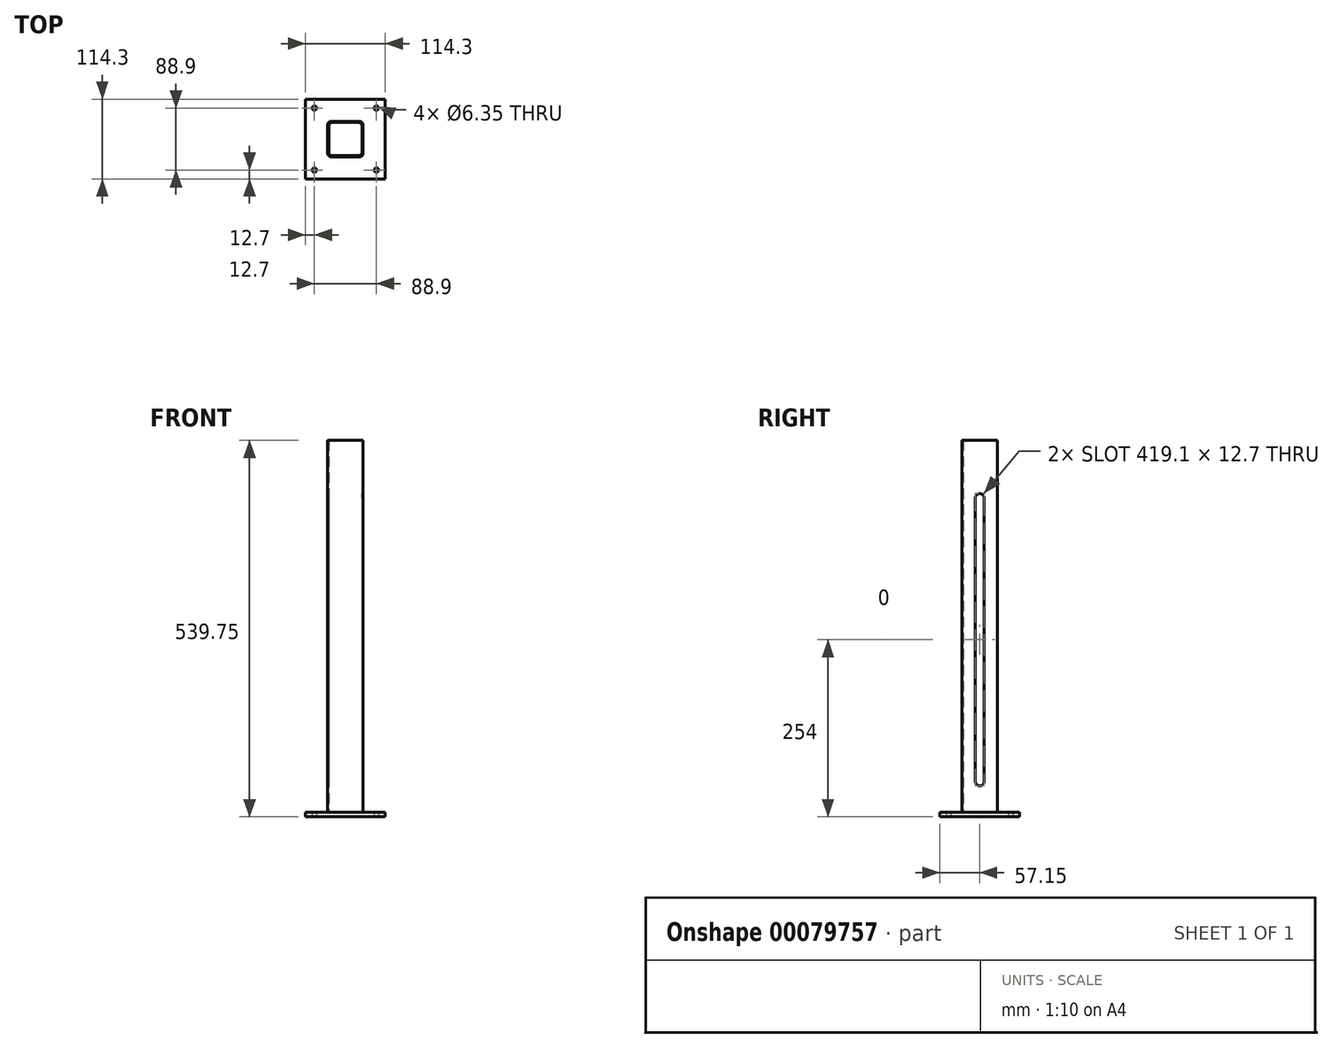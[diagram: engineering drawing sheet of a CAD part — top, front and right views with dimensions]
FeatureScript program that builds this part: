
annotation { "Feature Type Name" : "Feature", "Feature Type Description" : "" }
export const myFeature = defineFeature(function(context is Context, id is Id, definition is map)
    precondition{}
    {
        {
            var Q0;
            Q0=qCreatedBy(makeId("Top.planeOp"),FACE);
            var sketch = newSketch(context, id + "F0", { "sketchPlane" : qUnion([Q0])});
            skPoint(sketch, "E0.middle", {"position": v(0, 0) * mm});
            skCircle(sketch, "E1", {"center": v(-44.45, 44.45) * mm, "radius": 3.18 * mm});
            skCircle(sketch, "E2", {"center": v(44.45, 44.45) * mm, "radius": 3.18 * mm});
            skCircle(sketch, "E3", {"center": v(44.45, -44.45) * mm, "radius": 3.18 * mm});
            skCircle(sketch, "E4", {"center": v(-44.45, -44.45) * mm, "radius": 3.18 * mm});
            skLineSegment(sketch, "E5.bottom", {"start": v(57.15, 57.15) * mm, "end": v(-57.15, 57.15) * mm});
            skLineSegment(sketch, "E5.top", {"start": v(57.15, -57.15) * mm, "end": v(-57.15, -57.15) * mm});
            skLineSegment(sketch, "E5.left", {"start": v(57.15, 57.15) * mm, "end": v(57.15, -57.15) * mm});
            skLineSegment(sketch, "E5.right", {"start": v(-57.15, 57.15) * mm, "end": v(-57.15, -57.15) * mm});
            skSolve(sketch);
        }
        {
            var Q0;
            Q0 = qSketchRegion(id + "F0", true);
            extrude(context, id + "F1", {"entities" : qUnion([Q0]), "depth" : 6.35 * mm});
        }
        {
            var Q0;
            Q0=makeQuery(id+"F1.opExtrude","CAP_FACE",FACE,{"disambiguationData":[OSD([sQuery(id+"F0.wireOp",EDGE,"E1"),sQuery(id+"F0.wireOp",EDGE,"E2"),sQuery(id+"F0.wireOp",EDGE,"E3"),sQuery(id+"F0.wireOp",EDGE,"E4"),sQuery(id+"F0.wireOp",EDGE,"E5.bottom"),sQuery(id+"F0.wireOp",EDGE,"E5.top"),sQuery(id+"F0.wireOp",EDGE,"E5.left"),sQuery(id+"F0.wireOp",EDGE,"E5.right")])],"isStart":false});
            var sketch = newSketch(context, id + "F2", { "sketchPlane" : qUnion([Q0])});
            skLineSegment(sketch, "E6.bottom", {"start": v(25.4, 25.4) * mm, "end": v(-25.4, 25.4) * mm});
            skLineSegment(sketch, "E6.top", {"start": v(25.4, -25.4) * mm, "end": v(-25.4, -25.4) * mm});
            skLineSegment(sketch, "E6.left", {"start": v(25.4, 25.4) * mm, "end": v(25.4, -25.4) * mm});
            skLineSegment(sketch, "E6.right", {"start": v(-25.4, 25.4) * mm, "end": v(-25.4, -25.4) * mm});
            skPoint(sketch, "E6.middle", {"position": v(0, 0) * mm});
            skLineSegment(sketch, "E7.bottom", {"start": v(23.81, 23.81) * mm, "end": v(-23.81, 23.81) * mm});
            skLineSegment(sketch, "E7.top", {"start": v(23.81, -23.81) * mm, "end": v(-23.81, -23.81) * mm});
            skLineSegment(sketch, "E7.left", {"start": v(23.81, 23.81) * mm, "end": v(23.81, -23.81) * mm});
            skLineSegment(sketch, "E7.right", {"start": v(-23.81, 23.81) * mm, "end": v(-23.81, -23.81) * mm});
            skSolve(sketch);
        }
        {
            var Q0;
            Q0 = qSketchRegion(id + "F2", true);
            extrude(context, id + "F3", {"entities" : qUnion([Q0]), "operationType" : NewBodyOperationType.ADD, "depth" : 533.4 * mm});
        }
        {
            var Q0;
            Q0=makeQuery(id+"F3.opExtrude","SWEPT_EDGE",EDGE,{"disambiguationData":[OSD([sQuery(id+"F2.wireOp",EDGE,"E6.bottom"),sQuery(id+"F2.wireOp",EDGE,"E6.left")])]});
            var Q1;
            Q1=makeQuery(id+"F3.opExtrude","SWEPT_EDGE",EDGE,{"disambiguationData":[OSD([sQuery(id+"F2.wireOp",EDGE,"E6.top"),sQuery(id+"F2.wireOp",EDGE,"E6.left")])]});
            var Q2;
            Q2=makeQuery(id+"F3.opExtrude","SWEPT_EDGE",EDGE,{"disambiguationData":[OSD([sQuery(id+"F2.wireOp",EDGE,"E6.bottom"),sQuery(id+"F2.wireOp",EDGE,"E6.right")])]});
            var Q3;
            Q3=makeQuery(id+"F3.opExtrude","SWEPT_EDGE",EDGE,{"disambiguationData":[OSD([sQuery(id+"F2.wireOp",EDGE,"E6.top"),sQuery(id+"F2.wireOp",EDGE,"E6.right")])]});
            var Q4;
            Q4=makeQuery(id+"F3.opExtrude","SWEPT_EDGE",EDGE,{"disambiguationData":[OSD([sQuery(id+"F2.wireOp",EDGE,"E7.top"),sQuery(id+"F2.wireOp",EDGE,"E7.right")])]});
            var Q5;
            Q5=makeQuery(id+"F3.opExtrude","SWEPT_EDGE",EDGE,{"disambiguationData":[OSD([sQuery(id+"F2.wireOp",EDGE,"E7.bottom"),sQuery(id+"F2.wireOp",EDGE,"E7.left")])]});
            var Q6;
            Q6=makeQuery(id+"F3.opExtrude","SWEPT_EDGE",EDGE,{"disambiguationData":[OSD([sQuery(id+"F2.wireOp",EDGE,"E7.bottom"),sQuery(id+"F2.wireOp",EDGE,"E7.right")])]});
            var Q7;
            Q7=makeQuery(id+"F3.opExtrude","SWEPT_EDGE",EDGE,{"disambiguationData":[OSD([sQuery(id+"F2.wireOp",EDGE,"E7.top"),sQuery(id+"F2.wireOp",EDGE,"E7.left")])]});
            fillet(context, id + "F4", {"entities" : qUnion([Q0, Q1, Q2, Q3, Q4, Q5, Q6, Q7]), "radius" : 5.08 * mm, "tangentPropagation" : true, "allowEdgeOverflow" : false});
        }
        {
            var Q0;
            Q0=makeQuery(id+"F3.opExtrude","SWEPT_FACE",FACE,{"disambiguationData":[OSD([sQuery(id+"F2.wireOp",EDGE,"E6.right")])]});
            var sketch = newSketch(context, id + "F5", { "sketchPlane" : qUnion([Q0])});
            skLineSegment(sketch, "E8.left", {"start": v(6.35, 50.8) * mm, "end": v(6.35, 457.2) * mm});
            skLineSegment(sketch, "E8.right", {"start": v(-6.35, 50.8) * mm, "end": v(-6.35, 457.2) * mm});
            skPoint(sketch, "E8.middle", {"position": v(0, 254) * mm});
            skArc(sketch, "E9", {"start": v(6.35, 457.2) * mm, "mid": v(0, 463.55) * mm, "end": v(-6.35, 457.2) * mm});
            skArc(sketch, "E10", {"start": v(-6.35, 50.8) * mm, "mid": v(0, 44.45) * mm, "end": v(6.35, 50.8) * mm});
            skSolve(sketch);
        }
        {
            var Q0;
            Q0 = qSketchRegion(id + "F5", true);
            extrude(context, id + "F6", {"entities" : qUnion([Q0]), "operationType" : NewBodyOperationType.REMOVE, "endBound" : BoundingType.THROUGH_ALL, "oppositeDirection" : true, "depth" : 25.4 * mm});
        }
    });
